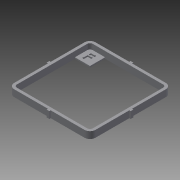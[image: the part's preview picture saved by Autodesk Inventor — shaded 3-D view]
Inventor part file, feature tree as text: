
AUTODESK INVENTOR PART (.ipt)
format: ipt  version: 2014 (Build 180170000, 170)  size: 143,872 bytes
history: native  units: mm
features: sketch x4, extrude x3, pattern_circular x1, fillet x1, shell x1, emboss x1
ambient origin geometry x8: Origin, YZ Plane, XZ Plane, XY Plane, X Axis, Y Axis, Z Axis, Center Point
bodies: Solid1 (feature_tree)
feature tree (11):
  extrude  "Extrusion1"  Depth=5.0mm TaperAngle=0.0deg
  extrude  "Extrusion2"  Depth=1.0mm
  pattern_circular  "Circular Pattern1"  Count=4 Angle=360.0deg
  fillet  "Fillet1"  Radius=4.0mm
  shell  "Shell1"  Thickness=2.0mm
  extrude  "Extrusion3"  Depth=1.0mm TaperAngle=0.0deg
  emboss  "Emboss1"
  sketch  "Sketch1"  dims[d0=60.0mm d1=5.0mm d2=0.0mm]
  sketch  "Sketch2"  dims[d3=2.0mm d4=1.0mm]
  sketch  "Sketch3"  dims[d5=0.0mm d6=0.0mm d7=40.0mm d8=360.0deg d10=4.0mm d11=2.0mm]
  sketch  "Sketch4"  dims[d12=12.0mm d13=1.0mm d14=0.0mm d15=1.0mm d16=1.0mm d17=1.0mm d18=0.0mm]
